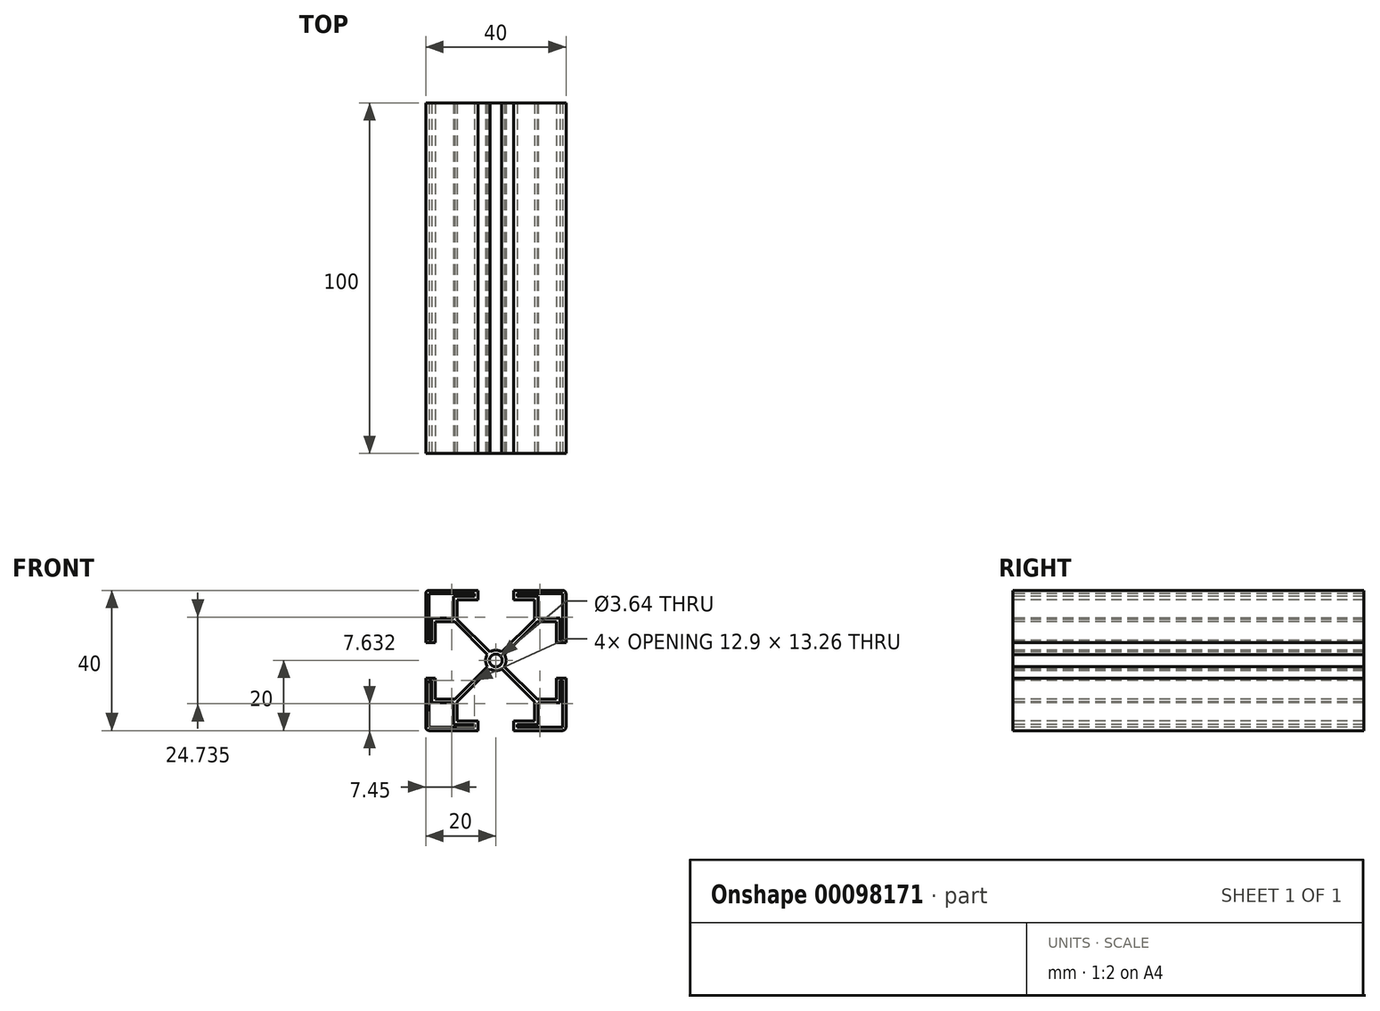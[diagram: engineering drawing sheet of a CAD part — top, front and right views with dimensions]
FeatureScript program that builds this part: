
annotation { "Feature Type Name" : "Feature", "Feature Type Description" : "" }
export const myFeature = defineFeature(function(context is Context, id is Id, definition is map)
    precondition{}
    {
        {
            var Q0;
            Q0=qCreatedBy(makeId("Front.planeOp"),FACE);
            var sketch = newSketch(context, id + "F0", { "sketchPlane" : qUnion([Q0])});
            skLineSegment(sketch, "E0", {"start": v(-60.76, 63.46) * mm, "end": v(-46.86, 63.46) * mm});
            skLineSegment(sketch, "E1", {"start": v(-61.76, 62.46) * mm, "end": v(-61.76, 48.56) * mm});
            skLineSegment(sketch, "E2", {"start": v(-41.76, 62.45) * mm, "end": v(-41.76, 5.18) * mm, "construction": true});
            skLineSegment(sketch, "E3", {"start": v(-69.79, 43.46) * mm, "end": v(51.08, 43.46) * mm, "construction": true});
            skLineSegment(sketch, "E4", {"start": v(-46.86, 63.46) * mm, "end": v(-46.86, 60.7) * mm});
            skLineSegment(sketch, "E5", {"start": v(-61.76, 48.56) * mm, "end": v(-59.01, 48.56) * mm});
            skLineSegment(sketch, "E6", {"start": v(-46.86, 60.7) * mm, "end": v(-52.86, 60.7) * mm});
            skLineSegment(sketch, "E7", {"start": v(-59.01, 48.56) * mm, "end": v(-59.01, 54.56) * mm});
            skLineSegment(sketch, "E8", {"start": v(-59.01, 54.56) * mm, "end": v(-53.51, 54.56) * mm});
            skLineSegment(sketch, "E9", {"start": v(-52.86, 60.7) * mm, "end": v(-52.86, 55.2) * mm});
            skLineSegment(sketch, "E10", {"start": v(-53.51, 54.56) * mm, "end": v(-44.12, 45.17) * mm});
            skLineSegment(sketch, "E11", {"start": v(-52.86, 55.2) * mm, "end": v(-43.47, 45.82) * mm});
            skLineSegment(sketch, "E12.MirrorCS", {"start": v(-36.66, 63.46) * mm, "end": v(-36.66, 60.7) * mm});
            skLineSegment(sketch, "E13.MirrorCS", {"start": v(-24.51, 54.56) * mm, "end": v(-30.01, 54.56) * mm});
            skLineSegment(sketch, "E14.MirrorCS", {"start": v(-21.76, 62.46) * mm, "end": v(-21.76, 48.56) * mm});
            skLineSegment(sketch, "E15.MirrorCS", {"start": v(-22.76, 63.46) * mm, "end": v(-36.66, 63.46) * mm});
            skLineSegment(sketch, "E16.MirrorCS", {"start": v(-30.01, 54.56) * mm, "end": v(-39.4, 45.17) * mm});
            skLineSegment(sketch, "E17.MirrorCS", {"start": v(-21.76, 48.56) * mm, "end": v(-24.51, 48.56) * mm});
            skLineSegment(sketch, "E18.MirrorCS", {"start": v(-24.51, 48.56) * mm, "end": v(-24.51, 54.56) * mm});
            skLineSegment(sketch, "E19.MirrorCS", {"start": v(-36.66, 60.7) * mm, "end": v(-30.66, 60.7) * mm});
            skLineSegment(sketch, "E20.MirrorCS", {"start": v(-30.66, 55.2) * mm, "end": v(-40.05, 45.82) * mm});
            skLineSegment(sketch, "E21.MirrorCS", {"start": v(-30.66, 60.7) * mm, "end": v(-30.66, 55.2) * mm});
            skLineSegment(sketch, "E22.MirrorCS", {"start": v(-22.76, 23.46) * mm, "end": v(-36.66, 23.46) * mm});
            skLineSegment(sketch, "E23.MirrorCS", {"start": v(-60.76, 23.46) * mm, "end": v(-46.86, 23.46) * mm});
            skLineSegment(sketch, "E24.MirrorCS", {"start": v(-30.66, 31.7) * mm, "end": v(-40.05, 41.1) * mm});
            skLineSegment(sketch, "E25.MirrorCS", {"start": v(-36.66, 26.2) * mm, "end": v(-30.66, 26.2) * mm});
            skLineSegment(sketch, "E26.MirrorCS", {"start": v(-36.66, 23.46) * mm, "end": v(-36.66, 26.2) * mm});
            skLineSegment(sketch, "E27.MirrorCS", {"start": v(-59.01, 32.36) * mm, "end": v(-53.51, 32.36) * mm});
            skLineSegment(sketch, "E28.MirrorCS", {"start": v(-59.01, 38.36) * mm, "end": v(-59.01, 32.36) * mm});
            skLineSegment(sketch, "E29.MirrorCS", {"start": v(-46.86, 26.2) * mm, "end": v(-52.86, 26.2) * mm});
            skLineSegment(sketch, "E30.MirrorCS", {"start": v(-21.76, 24.46) * mm, "end": v(-21.76, 38.36) * mm});
            skLineSegment(sketch, "E31.MirrorCS", {"start": v(-30.01, 32.36) * mm, "end": v(-39.4, 41.75) * mm});
            skLineSegment(sketch, "E32.MirrorCS", {"start": v(-24.51, 38.36) * mm, "end": v(-24.51, 32.36) * mm});
            skLineSegment(sketch, "E33.MirrorCS", {"start": v(-52.86, 26.2) * mm, "end": v(-52.86, 31.7) * mm});
            skLineSegment(sketch, "E34.MirrorCS", {"start": v(-46.86, 23.46) * mm, "end": v(-46.86, 26.2) * mm});
            skLineSegment(sketch, "E35.MirrorCS", {"start": v(-21.76, 38.36) * mm, "end": v(-24.51, 38.36) * mm});
            skLineSegment(sketch, "E36.MirrorCS", {"start": v(-53.51, 32.36) * mm, "end": v(-44.12, 41.75) * mm});
            skLineSegment(sketch, "E37.MirrorCS", {"start": v(-30.66, 26.2) * mm, "end": v(-30.66, 31.7) * mm});
            skLineSegment(sketch, "E38.MirrorCS", {"start": v(-52.86, 31.7) * mm, "end": v(-43.47, 41.1) * mm});
            skLineSegment(sketch, "E39.MirrorCS", {"start": v(-61.76, 38.36) * mm, "end": v(-59.01, 38.36) * mm});
            skLineSegment(sketch, "E40.MirrorCS", {"start": v(-61.76, 24.46) * mm, "end": v(-61.76, 38.36) * mm});
            skLineSegment(sketch, "E41.MirrorCS", {"start": v(-24.51, 32.36) * mm, "end": v(-30.01, 32.36) * mm});
            skArc(sketch, "E42", {"start": v(-43.47, 41.1) * mm, "mid": v(-41.76, 40.54) * mm, "end": v(-40.05, 41.1) * mm});
            skPoint(sketch, "E43.orphan", {"position": v(-41.76, 44.1) * mm});
            skPoint(sketch, "E44.orphan", {"position": v(-41.11, 43.46) * mm});
            skPoint(sketch, "E45.orphan", {"position": v(-41.76, 42.8) * mm});
            skPoint(sketch, "E46.orphan", {"position": v(-42.41, 43.46) * mm});
            skArc(sketch, "E47.trimOffspring", {"start": v(-44.12, 45.17) * mm, "mid": v(-44.68, 43.46) * mm, "end": v(-44.12, 41.75) * mm});
            skArc(sketch, "E48.trimOffspring", {"start": v(-40.05, 45.82) * mm, "mid": v(-41.76, 46.38) * mm, "end": v(-43.47, 45.82) * mm});
            skArc(sketch, "E49.trimOffspring", {"start": v(-39.4, 41.75) * mm, "mid": v(-38.84, 43.46) * mm, "end": v(-39.4, 45.17) * mm});
            skLineSegment(sketch, "E50", {"start": v(-60.76, 62.46) * mm, "end": v(-60.76, 55.56) * mm});
            skLineSegment(sketch, "E51", {"start": v(-60.01, 55.56) * mm, "end": v(-53.86, 55.56) * mm});
            skLineSegment(sketch, "E52", {"start": v(-53.86, 55.56) * mm, "end": v(-53.86, 61.7) * mm});
            skLineSegment(sketch, "E53", {"start": v(-53.86, 62.46) * mm, "end": v(-60.76, 62.46) * mm});
            skLineSegment(sketch, "E54", {"start": v(-60.76, 55.56) * mm, "end": v(-60.76, 49.2) * mm});
            skLineSegment(sketch, "E55", {"start": v(-60.76, 49.2) * mm, "end": v(-60.01, 49.2) * mm});
            skLineSegment(sketch, "E56", {"start": v(-60.01, 49.2) * mm, "end": v(-60.01, 55.56) * mm});
            skLineSegment(sketch, "E57", {"start": v(-53.86, 62.46) * mm, "end": v(-47.86, 62.46) * mm});
            skLineSegment(sketch, "E58", {"start": v(-47.86, 62.46) * mm, "end": v(-47.86, 61.7) * mm});
            skLineSegment(sketch, "E59", {"start": v(-47.86, 61.7) * mm, "end": v(-53.86, 61.7) * mm});
            skLineSegment(sketch, "E60.MirrorCS", {"start": v(-22.76, 62.46) * mm, "end": v(-22.76, 55.56) * mm});
            skLineSegment(sketch, "E61.MirrorCS", {"start": v(-22.76, 55.56) * mm, "end": v(-22.76, 49.2) * mm});
            skLineSegment(sketch, "E62.MirrorCS", {"start": v(-22.76, 49.2) * mm, "end": v(-23.51, 49.2) * mm});
            skLineSegment(sketch, "E63.MirrorCS", {"start": v(-23.51, 49.2) * mm, "end": v(-23.51, 55.56) * mm});
            skLineSegment(sketch, "E64.MirrorCS", {"start": v(-23.51, 55.56) * mm, "end": v(-29.66, 55.56) * mm});
            skLineSegment(sketch, "E65.MirrorCS", {"start": v(-29.66, 55.56) * mm, "end": v(-29.66, 61.7) * mm});
            skLineSegment(sketch, "E66.MirrorCS", {"start": v(-35.66, 61.7) * mm, "end": v(-29.66, 61.7) * mm});
            skLineSegment(sketch, "E67.MirrorCS", {"start": v(-35.66, 62.46) * mm, "end": v(-35.66, 61.7) * mm});
            skLineSegment(sketch, "E68.MirrorCS", {"start": v(-29.66, 62.46) * mm, "end": v(-22.76, 62.46) * mm});
            skLineSegment(sketch, "E69.MirrorCS", {"start": v(-29.66, 62.46) * mm, "end": v(-35.66, 62.46) * mm});
            skLineSegment(sketch, "E70.MirrorCS", {"start": v(-35.66, 24.46) * mm, "end": v(-35.66, 25.2) * mm});
            skLineSegment(sketch, "E71.MirrorCS", {"start": v(-22.76, 37.72) * mm, "end": v(-23.51, 37.72) * mm});
            skLineSegment(sketch, "E72.MirrorCS", {"start": v(-22.76, 31.36) * mm, "end": v(-22.76, 37.72) * mm});
            skLineSegment(sketch, "E73.MirrorCS", {"start": v(-23.51, 37.72) * mm, "end": v(-23.51, 31.36) * mm});
            skLineSegment(sketch, "E74.MirrorCS", {"start": v(-23.51, 31.36) * mm, "end": v(-29.66, 31.36) * mm});
            skLineSegment(sketch, "E75.MirrorCS", {"start": v(-22.76, 24.46) * mm, "end": v(-22.76, 31.36) * mm});
            skLineSegment(sketch, "E76.MirrorCS", {"start": v(-29.66, 31.36) * mm, "end": v(-29.66, 25.2) * mm});
            skLineSegment(sketch, "E77.MirrorCS", {"start": v(-35.66, 25.2) * mm, "end": v(-29.66, 25.2) * mm});
            skLineSegment(sketch, "E78.MirrorCS", {"start": v(-29.66, 24.46) * mm, "end": v(-35.66, 24.46) * mm});
            skLineSegment(sketch, "E79.MirrorCS", {"start": v(-29.66, 24.46) * mm, "end": v(-22.76, 24.46) * mm});
            skLineSegment(sketch, "E80.MirrorCS", {"start": v(-60.01, 37.72) * mm, "end": v(-60.01, 31.36) * mm});
            skLineSegment(sketch, "E81.MirrorCS", {"start": v(-60.76, 31.36) * mm, "end": v(-60.76, 37.72) * mm});
            skLineSegment(sketch, "E82.MirrorCS", {"start": v(-60.76, 37.72) * mm, "end": v(-60.01, 37.72) * mm});
            skLineSegment(sketch, "E83.MirrorCS", {"start": v(-60.01, 31.36) * mm, "end": v(-53.86, 31.36) * mm});
            skLineSegment(sketch, "E84.MirrorCS", {"start": v(-53.86, 31.36) * mm, "end": v(-53.86, 25.2) * mm});
            skLineSegment(sketch, "E85.MirrorCS", {"start": v(-47.86, 25.2) * mm, "end": v(-53.86, 25.2) * mm});
            skLineSegment(sketch, "E86.MirrorCS", {"start": v(-47.86, 24.46) * mm, "end": v(-47.86, 25.2) * mm});
            skLineSegment(sketch, "E87.MirrorCS", {"start": v(-53.86, 24.46) * mm, "end": v(-47.86, 24.46) * mm});
            skLineSegment(sketch, "E88.MirrorCS", {"start": v(-60.76, 24.46) * mm, "end": v(-60.76, 31.36) * mm});
            skLineSegment(sketch, "E89.MirrorCS", {"start": v(-53.86, 24.46) * mm, "end": v(-60.76, 24.46) * mm});
            skPoint(sketch, "E90.visualSharp", {"position": v(-61.76, 63.46) * mm});
            skArc(sketch, "E90.filletArc", {"start": v(-60.76, 63.46) * mm, "mid": v(-61.47, 63.17) * mm, "end": v(-61.76, 62.46) * mm});
            skPoint(sketch, "E91.visualSharp", {"position": v(-21.76, 63.46) * mm});
            skArc(sketch, "E91.filletArc", {"start": v(-21.76, 62.46) * mm, "mid": v(-22.05, 63.17) * mm, "end": v(-22.76, 63.46) * mm});
            skPoint(sketch, "E92.visualSharp", {"position": v(-21.76, 23.46) * mm});
            skArc(sketch, "E92.filletArc", {"start": v(-22.76, 23.46) * mm, "mid": v(-22.05, 23.75) * mm, "end": v(-21.76, 24.46) * mm});
            skPoint(sketch, "E93.visualSharp", {"position": v(-61.76, 23.46) * mm});
            skArc(sketch, "E93.filletArc", {"start": v(-61.76, 24.46) * mm, "mid": v(-61.47, 23.75) * mm, "end": v(-60.76, 23.46) * mm});
            skCircle(sketch, "E94", {"center": v(-41.76, 43.46) * mm, "radius": 1.82 * mm});
            skSolve(sketch);
        }
        {
            var Q0;
            Q0=makeQuery(id+"F0.imprint","IMPRINT",FACE,{"disambiguationData":[TD([[makeQuery(id+"F0.imprint","IMPRINT",EDGE,{"derivedFrom":sQuery(id+"F0.wireOp",EDGE,"E0")}),-1.0]])]});
            extrude(context, id + "F1", {"entities" : qUnion([Q0]), "oppositeDirection" : true, "depth" : 100 * mm});
        }
    });
